# Revit family: HL_condensate trap_HL138NH
name_source: partatom
category: Příslušenství trubek
units: mm (PartAtom-declared; Revit-internal decimal feet)

## family parameters
Kóta kulaté spojky = Použít průměr
Nadpis OmniClass = General Pipework and Ductwork Products
Ořezat dutým tvarem při načtení = Ne
Sdílené = Ne
Typ dílu = Normální
Vždy vertikální = Ano
Založené na pracovní rovině = Ne
Číslo OmniClass = 23.60.30.00

## types (1)
- HL_condensate trap_HL138NH
    CAPACITY = 0,033 l/s
    Cena = 0 $
    DIMENSION = DN32
    EAN = 9003076051915
    FLOW = 0.0 m³/h
    INLET = Ø 20 - 32 mm
    INSTALLATION HEIGHT = 60 - 110 mm
    Komentáře k typům = In-wall siphon for condensate water with hygienic adapter
    MATERIAL = PP
    Material = Plactic - White
    Material 2 = Plactic - Black
    Material 3 = Plastic - Red
    Model = HL138NH
    NOMINAL DIAMETER 2 = 32 mm
    Popis = Air condition and ventilation
    URL = http://www.hutterer-lechner.com
    Výchozí výška = 0 mm  [stored 0 ft]
    Výrobce = HL Hutterer & Lechner GmbH
    WEIGHT = 0,3 kg

note: [stored X ft] marks values corroborated as IEEE doubles in the binary element streams (Revit-internal decimal feet)
